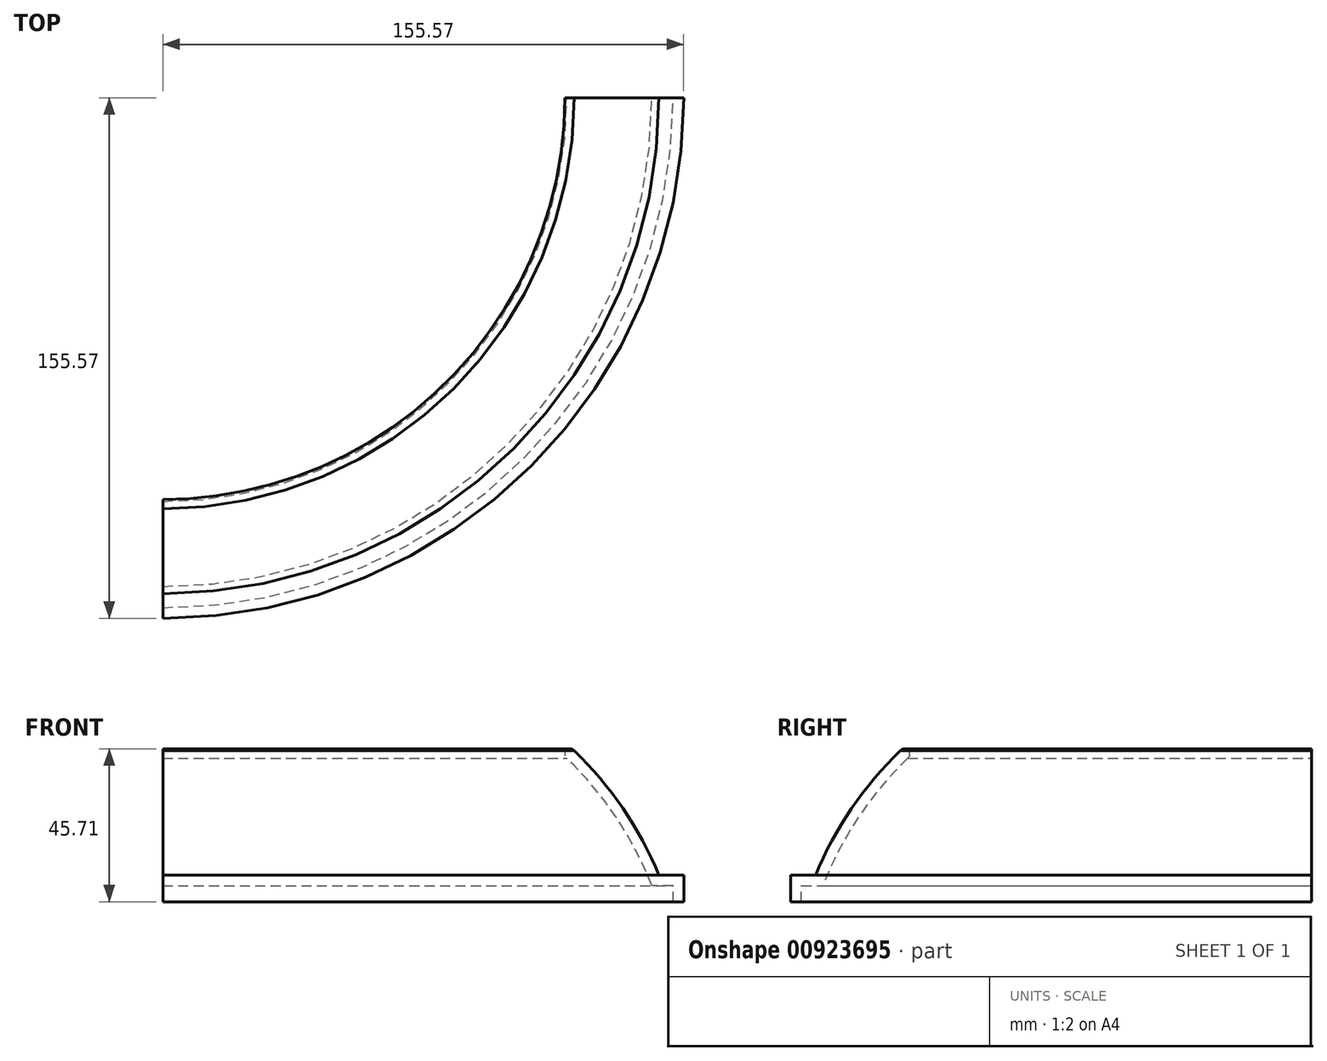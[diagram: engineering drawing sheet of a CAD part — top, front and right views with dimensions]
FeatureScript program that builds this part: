
annotation { "Feature Type Name" : "Feature", "Feature Type Description" : "" }
export const myFeature = defineFeature(function(context is Context, id is Id, definition is map)
    precondition{}
    {
        {
            var Q0;
            Q0=qCreatedBy(makeId("Front.planeOp"),FACE);
            var sketch = newSketch(context, id + "F0", { "sketchPlane" : qUnion([Q0])});
            skLineSegment(sketch, "E0", {"start": v(152.4, 0) * mm, "end": v(152.4, 4.76) * mm});
            skLineSegment(sketch, "E1", {"start": v(152.4, 4.76) * mm, "end": v(146.05, 4.76) * mm});
            skArc(sketch, "E2", {"start": v(146.05, 4.76) * mm, "mid": v(135.41, 25.19) * mm, "end": v(120.65, 42.86) * mm});
            skArc(sketch, "E3.0", {"start": v(148.2, 7.94) * mm, "mid": v(137.45, 27.85) * mm, "end": v(122.85, 45.15) * mm});
            skLineSegment(sketch, "E3.1", {"start": v(155.57, 7.94) * mm, "end": v(148.2, 7.94) * mm});
            skLineSegment(sketch, "E3.2", {"start": v(155.57, 0) * mm, "end": v(155.57, 7.94) * mm});
            skArc(sketch, "E4", {"start": v(122.85, 45.15) * mm, "mid": v(120.49, 45.22) * mm, "end": v(120.65, 42.86) * mm});
            skLineSegment(sketch, "E5", {"start": v(152.4, 0) * mm, "end": v(155.57, 0) * mm});
            skLineSegment(sketch, "E6", {"start": v(0, 33.13) * mm, "end": v(0, 10.06) * mm});
            skSolve(sketch);
        }
        {
            var Q0;
            Q0=makeQuery(id+"F0.imprint","IMPRINT",FACE,{"disambiguationData":[TD([[makeQuery(id+"F0.imprint","IMPRINT",EDGE,{"derivedFrom":sQuery(id+"F0.wireOp",EDGE,"E0")}),-1.0]])]});
            var Q1;
            Q1=sQuery(id+"F0.wireOp",EDGE,"E6");
            revolve(context, id + "F1", {"surfaceOperationType" : NewSurfaceOperationType.NEW, "entities" : qUnion([Q0]), "axis" : qUnion([Q1]), "revolveType" : RevolveType.ONE_DIRECTION, "angle" : 90 * degree});
        }
    });
